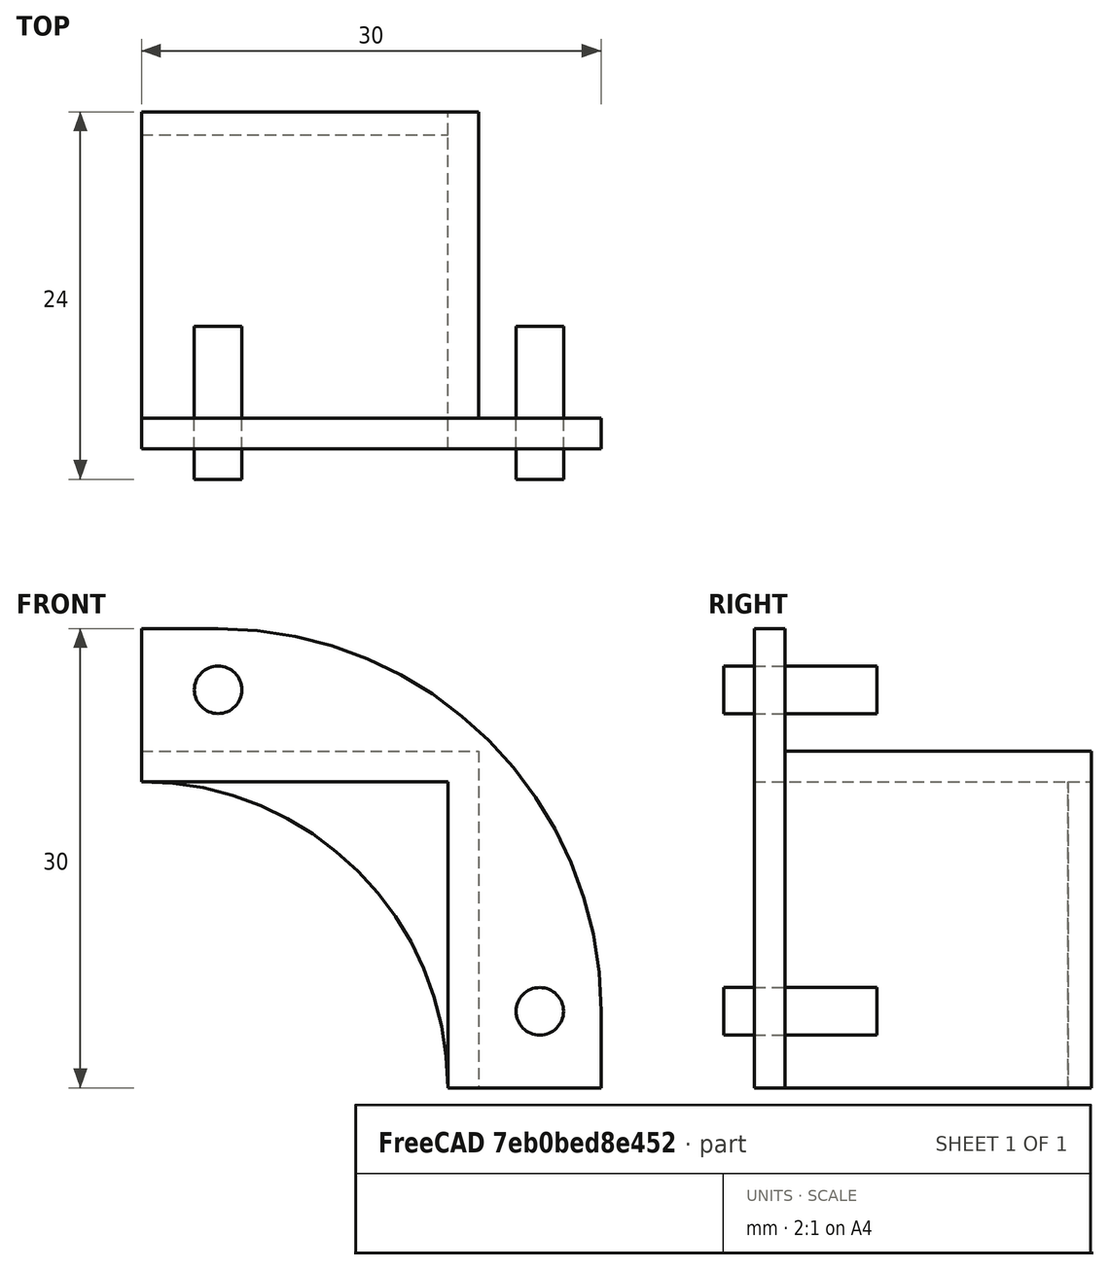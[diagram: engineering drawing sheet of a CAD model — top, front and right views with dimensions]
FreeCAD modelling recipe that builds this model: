
FCSTD DOCUMENT  (FreeCAD 0.17R13541 (Git))
Label: Sujetador
License: All rights reserved
LicenseURL: http://en.wikipedia.org/wiki/All_rights_reserved
objects: Part::Box×3, Part::Cylinder×3, Part::Cut×2, Part::MultiFuse×1, Part::Fillet×1
note: 10 computed .brp shape members not serialized (recipe doc carries the construction recipe); baked Part::Feature solids carry a one-line shape summary decoded from their .brp

FEATURE [Part::Box] Box  label="Cubo"
  AttacherType = Attacher::AttachEngine3D
  Height = 22
  Length = 22
  Width = 22
FEATURE [Part::Box] Box001  label="Cubo001"
  AttacherType = Attacher::AttachEngine3D
  Height = 20
  Length = 20
  Width = 20.5
FEATURE [Part::Box] Box002  label="Cubo002"
  AttacherType = Attacher::AttachEngine3D
  Height = 30
  Length = 30
  Width = 2
FEATURE [Part::MultiFuse] Fusion
  Refine = true
  Shapes = -> [Box002,Box]
FEATURE [Part::Cut] Cut
  Base = -> Fusion
  Refine = true
  Tool = -> Box001
FEATURE [Part::Fillet] Fillet
  Base = -> Cut
  Edges = 1 edges r=25: [Edge3]
FEATURE [Part::Cylinder] Cylinder  label="Cilindro"
  Angle = 360
  AttacherType = Attacher::AttachEngine3D
  Height = 10
  Placement = pos=(26,-2,5) rot=(-1,0,0;1.5708rad)
  Radius = 1.55
FEATURE [Part::Cylinder] Cylinder001  label="Cilindro001"
  Angle = 360
  AttacherType = Attacher::AttachEngine3D
  Height = 25
  Placement = pos=(0,0,0) rot=(-1,0,0;1.5708rad)
  Radius = 20
FEATURE [Part::Cut] Cut001
  Base = -> Fillet
  Refine = true
  Tool = -> Cylinder001
FEATURE [Part::Cylinder] Cylinder002  label="Cilindro002"
  Angle = 360
  AttacherType = Attacher::AttachEngine3D
  Height = 10
  Placement = pos=(5,-2,26) rot=(-1,0,0;1.5708rad)
  Radius = 1.55
